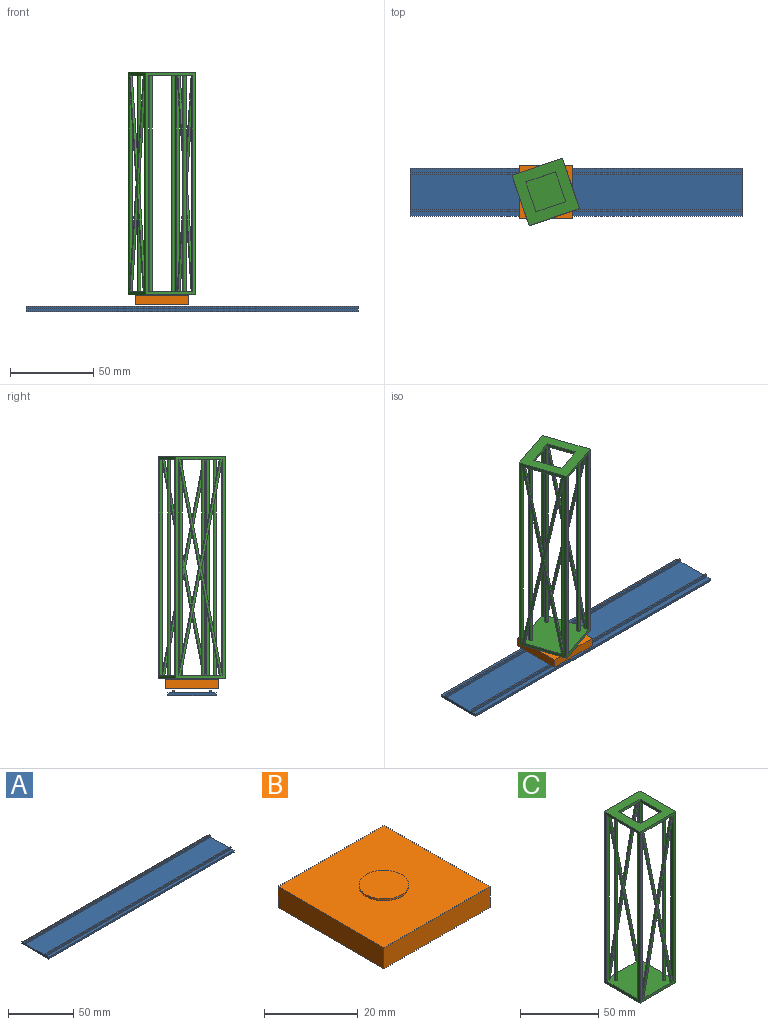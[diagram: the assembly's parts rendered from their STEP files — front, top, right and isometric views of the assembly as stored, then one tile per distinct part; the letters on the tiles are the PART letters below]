
ASSEMBLY  parts=3 mates=2
PART A: 14 faces, bbox 200x29.1x3.2 mm
  f0: plane 200x29.08mm, normal (0,0,-1), area 5816.8mm2, adj f1,f11,f12,f13
  f1: plane 200x1.54mm, normal (0,1,0), area 307.1mm2, adj f0,f2,f12,f13
  f2: plane 200x2.95mm, normal (0,0,1), area 589.7mm2, adj f1,f3,f12,f13
  f3: plane 200x1.68mm, normal (0,1,0), area 335mm2, adj f2,f4,f12,f13
  f4: plane 200x1.01mm, normal (0,0,1), area 201mm2, adj f3,f5,f12,f13
  f5: plane 200x1.68mm, normal (0,-1,0), area 335mm2, adj f4,f6,f12,f13
  f6: plane 200x21.18mm, normal (0,0,1), area 4235.4mm2, adj f5,f7,f12,f13
  f7: plane 200x1.68mm, normal (0,1,0), area 335mm2, adj f6,f8,f12,f13
  f8: plane 200x1.01mm, normal (0,0,1), area 201mm2, adj f7,f9,f12,f13
  f9: plane 200x1.68mm, normal (0,-1,0), area 335mm2, adj f8,f10,f12,f13
  f10: plane 200x2.95mm, normal (0,0,1), area 589.7mm2, adj f9,f11,f12,f13
  f11: plane 200x1.54mm, normal (0,-1,0), area 307.1mm2, adj f0,f10,f12,f13
  f12: plane 29.08x3.21mm, normal (1,0,0), area 48mm2, adj f0,f1,f2,f3,f4,f5,f6,f7
  f13: plane 29.08x3.21mm, normal (-1,0,0), area 48mm2, adj f0,f1,f2,f3,f4,f5,f6,f7
PART B: 8 faces, bbox 32x32x6 mm
  f0: plane 32x32mm, normal (0,0,-1), area 1024mm2, adj f1,f3,f4,f5
  f1: plane 32x5.46mm, normal (0,1,0), area 174.7mm2, adj f0,f2,f4,f5
  f2: plane 32x32mm, normal (0,0,1), area 935.5mm2, adj f1,f3,f4,f5,f6
  f3: plane 32x5.46mm, normal (0,-1,0), area 174.7mm2, adj f0,f2,f4,f5
  f4: plane 32x5.46mm, normal (1,0,0), area 174.7mm2, adj f0,f1,f2,f3
  f5: plane 32x5.46mm, normal (-1,0,0), area 174.7mm2, adj f0,f1,f2,f3
  f6: cylinder r=5.31mm len=10.61mm, axis (0,0,-1), area 16.7mm2, adj f2,f7
  f7: plane 10.61x10.61mm, normal (0,0,1), area 88.5mm2, adj f6
PART C: 42 faces, bbox 32x32x134 mm
  f0: plane 32x32mm, normal (0,0,1), area 986.4mm2, adj f2,f3,f4,f5,f7,f8,f9,f10
  f1: plane 32x32mm, normal (0,0,-1), area 625.4mm2, adj f2,f3,f4,f5,f7,f8,f9,f10
  f2: plane 134x32mm, normal (1,0,0), area 648mm2, adj f0,f1,f4,f5,f6,f13,f17,f23
  f3: plane 134x32mm, normal (-1,0,0), area 648mm2, adj f0,f1,f4,f5,f6,f7,f11,f23
  f4: plane 134x32mm, normal (0,-1,0), area 1032.5mm2, adj f0,f1,f2,f3,f6,f8,f18,f23
  f5: plane 134x32mm, normal (0,1,0), area 1032.5mm2, adj f0,f1,f2,f3,f6,f10,f14,f23
  f6: plane 32x32mm, normal (0,0,-1), area 1024mm2, adj f2,f3,f4,f5
  f7: plane 130x2mm, normal (0,1,0), area 260mm2, adj f0,f1,f3,f8
  f8: plane 130x2mm, normal (1,0,0), area 260mm2, adj f0,f1,f4,f7,f24,f31
  f9: cylinder r=1mm len=130mm, axis (0,0,-1), area 816.8mm2, adj f0,f1
  f10: plane 130x2mm, normal (1,0,0), area 260mm2, adj f0,f1,f5,f11,f37,f38
  f11: plane 130x2mm, normal (0,-1,0), area 260mm2, adj f0,f1,f3,f10
  f12: cylinder r=1mm len=130mm, axis (0,0,-1), area 816.8mm2, adj f0,f1
  f13: plane 130x2mm, normal (0,-1,0), area 260mm2, adj f0,f1,f2,f14
  f14: plane 130x2mm, normal (-1,0,0), area 260mm2, adj f0,f1,f5,f13,f33,f34
  f15: cylinder r=1mm len=130mm, axis (0,0,-1), area 816.8mm2, adj f0,f1
  f16: cylinder r=1mm len=130mm, axis (0,0,-1), area 816.8mm2, adj f0,f1
  f17: plane 130x2mm, normal (0,1,0), area 260mm2, adj f0,f1,f2,f18
  f18: plane 130x2mm, normal (-1,0,0), area 260mm2, adj f0,f1,f4,f17,f27,f28
  f19: plane 19x2mm, normal (1,0,0), area 38mm2, adj f1,f20,f22,f23
  f20: plane 19x2mm, normal (0,-1,0), area 38mm2, adj f1,f19,f21,f23
  f21: plane 19x2mm, normal (-1,0,0), area 38mm2, adj f1,f20,f22,f23
  f22: plane 19x2mm, normal (0,1,0), area 38mm2, adj f1,f19,f21,f23
  f23: plane 32x32mm, normal (0,0,1), area 663mm2, adj f2,f3,f4,f5,f19,f20,f21,f22
  f24: plane 65x13.25mm, normal (-0.98,0,0.2), area 99.5mm2, adj f4,f8,f31,f32
  f25: plane 61.32x12.5mm, normal (0.98,0,-0.2), area 93.9mm2, adj f0,f4,f26,f32
  f26: plane 61.32x12.5mm, normal (-0.98,0,-0.2), area 93.9mm2, adj f0,f4,f25,f32
  f27: plane 65x13.25mm, normal (0.98,0,0.2), area 99.5mm2, adj f4,f18,f28,f32
  f28: plane 65x13.25mm, normal (0.98,0,-0.2), area 99.5mm2, adj f4,f18,f27,f32
  f29: plane 61.32x12.5mm, normal (-0.98,0,0.2), area 93.9mm2, adj f1,f4,f30,f32
  f30: plane 61.32x12.5mm, normal (0.98,0,0.2), area 93.9mm2, adj f1,f4,f29,f32
  f31: plane 65x13.25mm, normal (-0.98,0,-0.2), area 99.5mm2, adj f4,f8,f24,f32
  f32: plane 130x28mm, normal (0,1,0), area 384.5mm2, adj f0,f1,f24,f25,f26,f27,f28,f29
  f33: plane 65x13.25mm, normal (0.98,0,-0.2), area 99.5mm2, adj f5,f14,f34,f41
  f34: plane 65x13.25mm, normal (0.98,0,0.2), area 99.5mm2, adj f5,f14,f33,f41
  f35: plane 61.32x12.5mm, normal (-0.98,0,-0.2), area 93.9mm2, adj f0,f5,f36,f41
  f36: plane 61.32x12.5mm, normal (0.98,0,-0.2), area 93.9mm2, adj f0,f5,f35,f41
  f37: plane 65x13.25mm, normal (-0.98,0,0.2), area 99.5mm2, adj f5,f10,f38,f41
  f38: plane 65x13.25mm, normal (-0.98,0,-0.2), area 99.5mm2, adj f5,f10,f37,f41
  f39: plane 61.32x12.5mm, normal (0.98,0,0.2), area 93.9mm2, adj f1,f5,f40,f41
  f40: plane 61.32x12.5mm, normal (-0.98,0,0.2), area 93.9mm2, adj f1,f5,f39,f41
  f41: plane 130x28mm, normal (0,-1,0), area 384.5mm2, adj f0,f1,f33,f34,f35,f36,f37,f38
PLACE A at identity fixed
PLACE B t=(65.76,0,-0.05)mm
PLACE C rot(axis=(0,0,1),108.7deg) t=(86.9,-15.15,-0.4)mm
MATE slider B.f5 <-> A.f13  axis (1,0,0) through (65.76,0,4.04)mm
MATE revolute C.f6 <-> B.f6  axis (0,0,-1) through (81.76,0,9.99)mm
